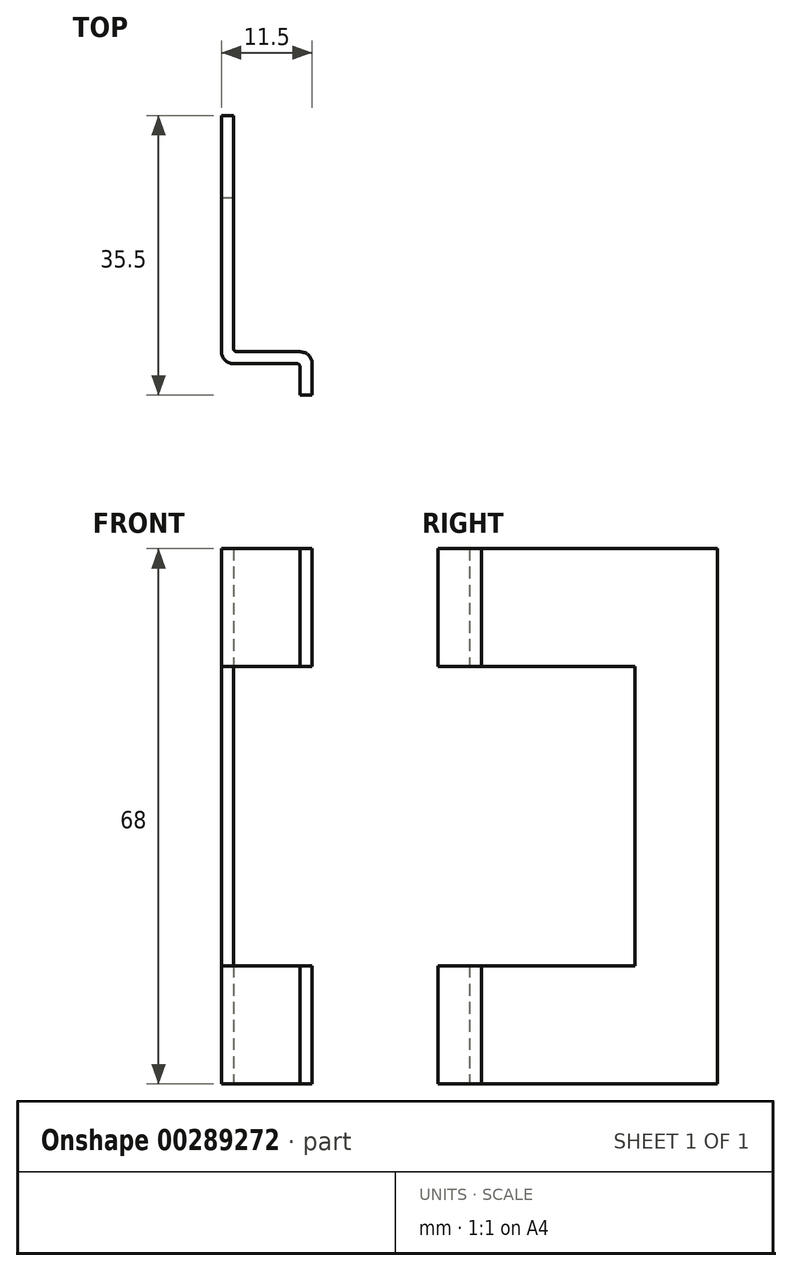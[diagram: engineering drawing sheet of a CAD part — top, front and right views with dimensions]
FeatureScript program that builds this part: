
annotation { "Feature Type Name" : "Feature", "Feature Type Description" : "" }
export const myFeature = defineFeature(function(context is Context, id is Id, definition is map)
    precondition{}
    {
        {
            var Q0;
            Q0=qCreatedBy(makeId("Top.planeOp"),FACE);
            var sketch = newSketch(context, id + "F0", { "sketchPlane" : qUnion([Q0])});
            skLineSegment(sketch, "E0", {"start": v(-1.5, 0) * mm, "end": v(-1.5, 4) * mm});
            skLineSegment(sketch, "E1", {"start": v(-1.5, 4) * mm, "end": v(-11.5, 4) * mm});
            skLineSegment(sketch, "E2", {"start": v(-11.5, 4) * mm, "end": v(-11.5, 35.5) * mm});
            skLineSegment(sketch, "E3", {"start": v(-11.5, 35.5) * mm, "end": v(-10, 35.5) * mm});
            skLineSegment(sketch, "E4", {"start": v(-10, 35.5) * mm, "end": v(-10, 5.5) * mm});
            skLineSegment(sketch, "E5", {"start": v(-10, 5.5) * mm, "end": v(0, 5.5) * mm});
            skLineSegment(sketch, "E6", {"start": v(0, 5.5) * mm, "end": v(0, 0) * mm});
            skLineSegment(sketch, "E7", {"start": v(0, 0) * mm, "end": v(-1.5, 0) * mm});
            skSolve(sketch);
        }
        {
            var Q0;
            Q0 = qSketchRegion(id + "F0", true);
            extrude(context, id + "F1", {"entities" : qUnion([Q0]), "endBound" : BoundingType.SYMMETRIC, "depth" : 68 * mm});
        }
        {
            var Q0;
            Q0=makeQuery(id+"F1.opExtrude","SWEPT_FACE",FACE,{"disambiguationData":[OSD([sQuery(id+"F0.wireOp",EDGE,"E2")])]});
            var sketch = newSketch(context, id + "F2", { "sketchPlane" : qUnion([Q0])});
            skLineSegment(sketch, "E8", {"start": v(0, -19) * mm, "end": v(-25, -19) * mm});
            skLineSegment(sketch, "E9", {"start": v(-25, -19) * mm, "end": v(-25, 19) * mm});
            skLineSegment(sketch, "E10", {"start": v(-25, 19) * mm, "end": v(0, 19) * mm});
            skLineSegment(sketch, "E11", {"start": v(0, 19) * mm, "end": v(0, -19) * mm});
            skSolve(sketch);
        }
        {
            var Q0;
            {var subQ0=sQuery(id+"F2.wireOp",EDGE,"E11");Q0=makeQuery(id+"F2.imprint","IMPRINT",FACE,{"disambiguationData":[TD([[makeQuery(id+"F2.imprint","IMPRINT",EDGE,{"derivedFrom":subQ0}),-1.0]])]});}
            var Q1;
            {var subQ0=sQuery(id+"F2.wireOp",EDGE,"E9");Q1=makeQuery(id+"F2.imprint","IMPRINT",FACE,{"disambiguationData":[TD([[makeQuery(id+"F2.imprint","IMPRINT",EDGE,{"derivedFrom":subQ0}),-1.0]])]});}
            extrude(context, id + "F3", {"entities" : qUnion([Q0, Q1]), "operationType" : NewBodyOperationType.REMOVE, "oppositeDirection" : true, "depth" : 50 * mm});
        }
        {
            var Q0;
            {var subQ0=sQuery(id+"F0.wireOp",EDGE,"E6");var subQ1=sQuery(id+"F0.wireOp",EDGE,"E5");Q0=makeQuery(id+"F3.boolean.opBoolean","SPLIT",EDGE,{"disambiguationData":[TD([makeQuery(id+"F3.opExtrude","SWEPT_FACE",FACE,{"disambiguationData":[OSD([sQuery(id+"F2.wireOp",EDGE,"E10")])]})])],"derivedFrom":makeQuery(id+"F1.opExtrude","SWEPT_EDGE",EDGE,{"disambiguationData":[OSD([subQ1,subQ0])]})});}
            var Q1;
            {var subQ0=sQuery(id+"F0.wireOp",EDGE,"E6");var subQ1=sQuery(id+"F0.wireOp",EDGE,"E5");Q1=makeQuery(id+"F3.boolean.opBoolean","SPLIT",EDGE,{"disambiguationData":[TD([makeQuery(id+"F3.opExtrude","SWEPT_FACE",FACE,{"disambiguationData":[OSD([sQuery(id+"F2.wireOp",EDGE,"E8")])]})])],"derivedFrom":makeQuery(id+"F1.opExtrude","SWEPT_EDGE",EDGE,{"disambiguationData":[OSD([subQ1,subQ0])]})});}
            var Q2;
            {var subQ0=sQuery(id+"F0.wireOp",EDGE,"E2");var subQ1=sQuery(id+"F0.wireOp",EDGE,"E1");Q2=makeQuery(id+"F3.boolean.opBoolean","SPLIT",EDGE,{"disambiguationData":[TD([makeQuery(id+"F3.opExtrude","SWEPT_FACE",FACE,{"disambiguationData":[OSD([sQuery(id+"F2.wireOp",EDGE,"E8")])]})])],"derivedFrom":makeQuery(id+"F1.opExtrude","SWEPT_EDGE",EDGE,{"disambiguationData":[OSD([subQ1,subQ0])]})});}
            var Q3;
            {var subQ0=sQuery(id+"F0.wireOp",EDGE,"E2");var subQ1=sQuery(id+"F0.wireOp",EDGE,"E1");Q3=makeQuery(id+"F3.boolean.opBoolean","SPLIT",EDGE,{"disambiguationData":[TD([makeQuery(id+"F3.opExtrude","SWEPT_FACE",FACE,{"disambiguationData":[OSD([sQuery(id+"F2.wireOp",EDGE,"E10")])]})])],"derivedFrom":makeQuery(id+"F1.opExtrude","SWEPT_EDGE",EDGE,{"disambiguationData":[OSD([subQ1,subQ0])]})});}
            fillet(context, id + "F4", {"entities" : qUnion([Q0, Q1, Q2, Q3]), "radius" : 1.5 * mm, "tangentPropagation" : true, "allowEdgeOverflow" : false});
        }
        {
            var Q0;
            {var subQ0=sQuery(id+"F0.wireOp",EDGE,"E5");var subQ1=sQuery(id+"F0.wireOp",EDGE,"E4");Q0=makeQuery(id+"F3.boolean.opBoolean","SPLIT",EDGE,{"disambiguationData":[TD([makeQuery(id+"F3.opExtrude","SWEPT_FACE",FACE,{"disambiguationData":[OSD([sQuery(id+"F2.wireOp",EDGE,"E8")])]})])],"derivedFrom":makeQuery(id+"F1.opExtrude","SWEPT_EDGE",EDGE,{"disambiguationData":[OSD([subQ1,subQ0])]})});}
            var Q1;
            {var subQ0=sQuery(id+"F0.wireOp",EDGE,"E5");var subQ1=sQuery(id+"F0.wireOp",EDGE,"E4");Q1=makeQuery(id+"F3.boolean.opBoolean","SPLIT",EDGE,{"disambiguationData":[TD([makeQuery(id+"F3.opExtrude","SWEPT_FACE",FACE,{"disambiguationData":[OSD([sQuery(id+"F2.wireOp",EDGE,"E10")])]})])],"derivedFrom":makeQuery(id+"F1.opExtrude","SWEPT_EDGE",EDGE,{"disambiguationData":[OSD([subQ1,subQ0])]})});}
            var Q2;
            {var subQ0=sQuery(id+"F0.wireOp",EDGE,"E0");var subQ1=sQuery(id+"F0.wireOp",EDGE,"E1");Q2=makeQuery(id+"F3.boolean.opBoolean","SPLIT",EDGE,{"disambiguationData":[TD([makeQuery(id+"F3.opExtrude","SWEPT_FACE",FACE,{"disambiguationData":[OSD([sQuery(id+"F2.wireOp",EDGE,"E8")])]})])],"derivedFrom":makeQuery(id+"F1.opExtrude","SWEPT_EDGE",EDGE,{"disambiguationData":[OSD([subQ0,subQ1])]})});}
            var Q3;
            {var subQ0=sQuery(id+"F0.wireOp",EDGE,"E0");var subQ1=sQuery(id+"F0.wireOp",EDGE,"E1");Q3=makeQuery(id+"F3.boolean.opBoolean","SPLIT",EDGE,{"disambiguationData":[TD([makeQuery(id+"F3.opExtrude","SWEPT_FACE",FACE,{"disambiguationData":[OSD([sQuery(id+"F2.wireOp",EDGE,"E10")])]})])],"derivedFrom":makeQuery(id+"F1.opExtrude","SWEPT_EDGE",EDGE,{"disambiguationData":[OSD([subQ0,subQ1])]})});}
            fillet(context, id + "F5", {"entities" : qUnion([Q0, Q1, Q2, Q3]), "radius" : 0.5 * mm, "tangentPropagation" : true, "allowEdgeOverflow" : false});
        }
    });
